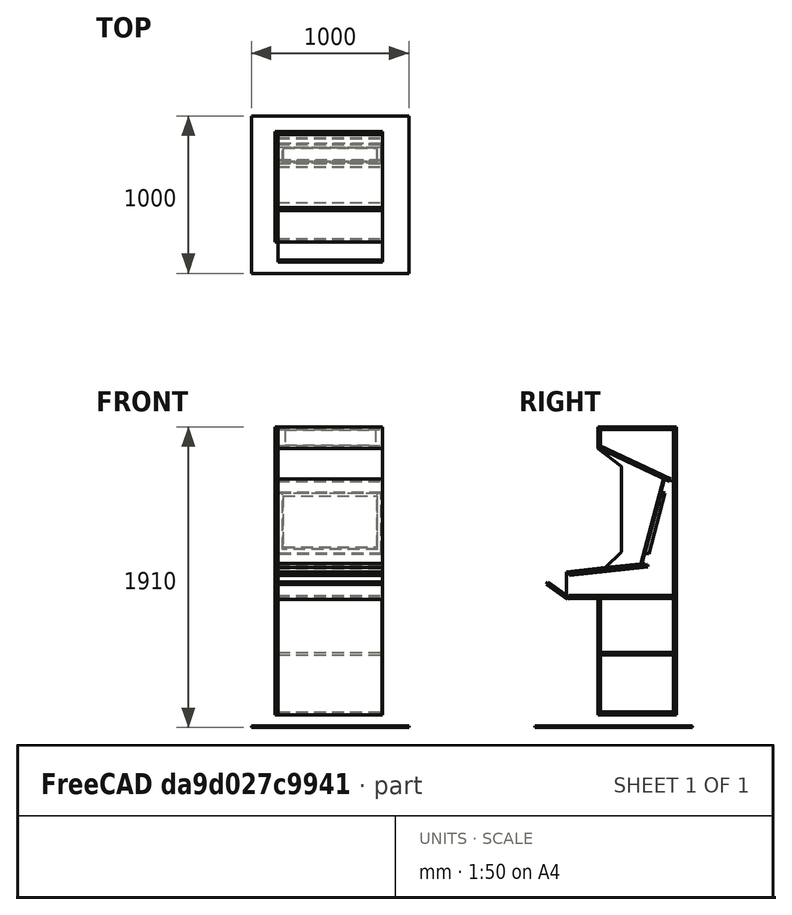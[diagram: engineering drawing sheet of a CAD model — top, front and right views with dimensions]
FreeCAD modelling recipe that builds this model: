
FCSTD DOCUMENT  (FreeCAD 0.14R3402 (Git))
Label: cabinet
License: CC-BY 3.0
LicenseURL: http://creativecommons.org/licenses/by/3.0/
objects: Part::Box×21, Part::Cut×2, App::DocumentObjectGroup×2, Sketcher::SketchObject×1, Part::Extrusion×1, Part::Mirroring×1
note: 26 computed .brp shape members not serialized (recipe doc carries the construction recipe); baked Part::Feature solids carry a one-line shape summary decoded from their .brp

FEATURE [Sketcher::SketchObject] Sketch
  Placement = pos=(0,0,0) rot=(0.57735,0.57735,0.57735;2.0944rad)
  sketch-geometry (11):
    g0: LineSegment StartX=-100 StartY=70 StartZ=0 EndX=400 EndY=70 EndZ=0
    g1: LineSegment StartX=-100 StartY=70 StartZ=0 EndX=-100 EndY=810 EndZ=0
    g2: LineSegment StartX=400 StartY=70 StartZ=0 EndX=400 EndY=1900 EndZ=0
    g3: LineSegment StartX=-100 StartY=810 StartZ=0 EndX=-300 EndY=810 EndZ=0
    g4: LineSegment StartX=-300 StartY=810 StartZ=0 EndX=-300 EndY=980 EndZ=0
    g5: LineSegment StartX=-300 StartY=980 StartZ=0 EndX=-50 EndY=1005.47 EndZ=0
    g6: LineSegment StartX=-50 StartY=1005.47 StartZ=0 EndX=50 EndY=1105 EndZ=0
    g7: LineSegment StartX=50 StartY=1105 StartZ=0 EndX=50 EndY=1650 EndZ=0
    g8: LineSegment StartX=50 StartY=1650 StartZ=0 EndX=-100 EndY=1765 EndZ=0
    g9: LineSegment StartX=-100 StartY=1765 StartZ=0 EndX=-100 EndY=1900 EndZ=0
    g10: LineSegment StartX=-100 StartY=1900 StartZ=0 EndX=400 EndY=1900 EndZ=0
  constraints (16):
    c: Horizontal(g0)
    c: Coincident(g1,g0)
    c: Vertical(g1)
    c: Coincident(g2,g0)
    c: Vertical(g2)
    c: Coincident(g3,g1)
    c: Coincident(g4,g3)
    c: Vertical(g4)
    c: Coincident(g5,g4)
    c: Coincident(g7,g6)
    c: Coincident(g8,g7)
    c: Coincident(g9,g8)
    c: Vertical(g9)
    c: Coincident(g10,g9)
    c: Horizontal(g10)
    c: Coincident(g2,g10)
FEATURE [Part::Extrusion] Extrude002  label="Right Panel"
  Base = -> Sketch
  Dir = (18,0,0)
  Placement = pos=(332,0,0) rot=(0,0,1;0rad)
  Solid = true
FEATURE [Part::Mirroring] Part__Mirroring  label="Left Panel"
  Base = (0.00012207,0,1000)
  Normal = (1,0,-1.19209e-07)
  Source = -> Extrude002
FEATURE [Part::Box] Box  label="Back"
  Height = 18
  Length = 664
  Placement = pos=(-332,400,70) rot=(1,0,0;1.5708rad)
  Width = 1830
FEATURE [Part::Box] Box002  label="Top Panel"
  Height = 3
  Length = 664
  Placement = pos=(-332,-100,1900) rot=(-1,0,0;1.5708rad)
  Width = 136
FEATURE [Part::Box] Box003  label="Top LED Matrix"
  Height = 15
  Length = 575
  Placement = pos=(-287.5,-97,1880) rot=(-1,0,0;1.5708rad)
  Width = 95
FEATURE [Part::Box] Box005  label="Cube"
  Height = 400
  Length = 648
  Placement = pos=(-324,0,0) rot=(0,0,1;0rad)
  Width = 25
FEATURE [Part::Box] Box006  label="Screen section"
  Height = 338
  Length = 598
  Placement = pos=(-299,-2,37) rot=(0,0,1;0rad)
  Width = 5
FEATURE [Part::Cut] Cut  label="Screen"
  Base = -> Box005
  Placement = pos=(0,200,1100) rot=(-1,0,0;0.261799rad)
  Tool = -> Box006
FEATURE [Part::Box] Box004  label="Room Floor"
  Height = 10
  Length = 1000
  Placement = pos=(-500,-500,-10) rot=(0,0,1;0rad)
  Width = 1000
FEATURE [Part::Box] Box007  label="Front Door"
  Height = 18
  Length = 662
  Placement = pos=(-331,-100,810) rot=(-1,0,0;1.5708rad)
  Width = 740
FEATURE [Part::Box] Box008  label="Floor"
  Height = 18
  Length = 664
  Placement = pos=(-332,-82,70) rot=(0,0,1;0rad)
  Width = 464
FEATURE [Part::Box] Box009  label="Roof"
  Height = 18
  Length = 664
  Placement = pos=(-332,-82,1882) rot=(0,0,1;0rad)
  Width = 464
FEATURE [Part::Box] Box010  label="Ceiling"
  Height = 18
  Length = 664
  Placement = pos=(-332,-97,1765) rot=(-1,0,0;0.436332rad)
  Width = 500
FEATURE [App::DocumentObjectGroup] Group  label="Main Panels"
  Group = -> [Extrude002,Part__Mirroring,Box,Box007,Box008,Box009,Box010]
FEATURE [Part::Box] Box011  label="Top Shelf"
  Height = 18
  Length = 664
  Placement = pos=(-332,-280,957) rot=(1,0,0;0.10472rad)
  Width = 500
FEATURE [Part::Box] Box012  label="Bottom Shelf"
  Height = 18
  Length = 664
  Placement = pos=(-332,-282,810) rot=(0,0,1;0rad)
  Width = 664
FEATURE [Part::Box] Box013  label="Keyboard Panel"
  Height = 18
  Length = 664
  Placement = pos=(-332,-282,820) rot=(1,0,0;2.53073rad)
  Width = 164
FEATURE [Part::Box] Box014  label="Main Shelf"
  Height = 18
  Length = 664
  Placement = pos=(-332,-82,450) rot=(0,0,1;0rad)
  Width = 464
FEATURE [Part::Box] Box015  label="Black Plexiglass"
  Height = 3
  Length = 664
  Placement = pos=(-332,-300,974) rot=(1,0,0;0.10472rad)
  Width = 250
FEATURE [Part::Box] Box016  label="Tranparent Plexiglass"
  Height = 3
  Length = 664
  Placement = pos=(-332,-300,977) rot=(1,0,0;0.10472rad)
  Width = 250
FEATURE [Part::Box] Box017  label="Filling 1"
  Height = 3
  Length = 664
  Placement = pos=(-332,-50,1000) rot=(1,0,0;0.10472rad)
  Width = 250
FEATURE [Part::Box] Box018  label="Filling 2"
  Height = 3
  Length = 664
  Placement = pos=(-332,-50,1003) rot=(1,0,0;0.10472rad)
  Width = 250
FEATURE [App::DocumentObjectGroup] Group001  label="Console"
  Group = -> [Box011,Box012,Box013,Box015,Box016,Box017,Box018]
FEATURE [Part::Box] Box019  label="Screen Protection"
  Height = 3
  Length = 664
  Placement = pos=(-332,177,1032) rot=(1,0,0;1.309rad)
  Width = 555
FEATURE [Part::Box] Box020  label="Screen Mask Panel"
  Height = 3
  Length = 664
  Placement = pos=(-332,180,1032) rot=(1,0,0;1.309rad)
  Width = 555
FEATURE [Part::Box] Box021  label="Screen Mask Cutout"
  Height = 30
  Length = 604
  Placement = pos=(-302,215,1120) rot=(1,0,0;1.309rad)
  Width = 365
FEATURE [Part::Cut] Cut001  label="Screen Mask"
  Base = -> Box020
  Tool = -> Box021
